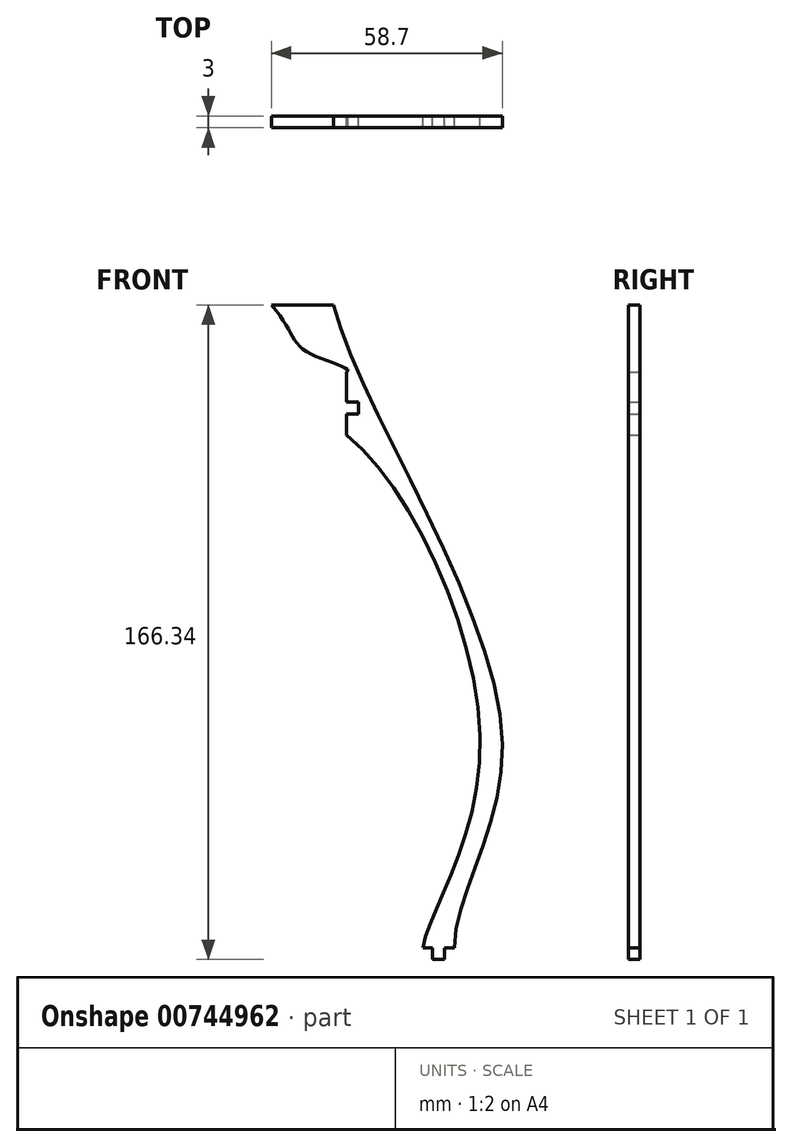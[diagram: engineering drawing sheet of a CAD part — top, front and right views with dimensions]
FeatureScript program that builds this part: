
annotation { "Feature Type Name" : "Feature", "Feature Type Description" : "" }
export const myFeature = defineFeature(function(context is Context, id is Id, definition is map)
    precondition{}
    {
        {
            var Q0;
            Q0=qCreatedBy(makeId("Front.planeOp"),FACE);
            var sketch = newSketch(context, id + "F0", { "sketchPlane" : qUnion([Q0])});
            skLineSegment(sketch, "E0", {"start": v(21.9, 51.28) * mm, "end": v(37.73, 51.28) * mm});
            skFitSpline(sketch, "E1", {"points": [v(37.73, 51.28) * mm, v(80.45, -57.24) * mm, v(68.38, -112.06) * mm], "startDerivative": vector(32.2, -132.18) * mm, "endDerivative": vector(-1.43, -110.43) * mm});
            skLineSegment(sketch, "E2", {"start": v(68.38, -112.06) * mm, "end": v(60.38, -112.06) * mm});
            skFitSpline(sketch, "E3", {"points": [v(0, 22.24) * mm, v(34.05, 22.24) * mm, v(74.9, -59.68) * mm, v(60.38, -112.06) * mm], "startDerivative": vector(163.27, -73.62) * mm, "endDerivative": vector(-14.47, -87.67) * mm});
            skLineSegment(sketch, "E4", {"start": v(41, 35) * mm, "end": v(41, 34.2) * mm});
            skLineSegment(sketch, "E5", {"start": v(41, 35) * mm, "end": v(41, 26.61) * mm});
            skPoint(sketch, "E6.start.orphan", {"position": v(0, 51.28) * mm});
            skPoint(sketch, "E7.orphan", {"position": v(0, 48.13) * mm});
            skPoint(sketch, "E8.start.orphan", {"position": v(0, 31.7) * mm});
            skLineSegment(sketch, "E9.bottom", {"start": v(41, 26.61) * mm, "end": v(44, 26.61) * mm});
            skLineSegment(sketch, "E9.top", {"start": v(41, 23.61) * mm, "end": v(44, 23.61) * mm});
            skLineSegment(sketch, "E9.right", {"start": v(44, 26.61) * mm, "end": v(44, 23.61) * mm});
            skLineSegment(sketch, "E10.trimOffspring", {"start": v(41, 23.61) * mm, "end": v(41, 18.21) * mm});
            skFitSpline(sketch, "E11", {"points": [v(21.9, 51.28) * mm, v(31.33, 39.12) * mm, v(41, 34.2) * mm], "startDerivative": vector(29.94, -33.73) * mm, "endDerivative": vector(-13.48, -6.74) * mm});
            skLineSegment(sketch, "E12", {"start": v(0, -62.73) * mm, "end": v(0, -105.6) * mm});
            skSolve(sketch);
        }
        {
            var Q0;
            Q0=makeQuery(id+"F0.imprint","IMPRINT",FACE,{"disambiguationData":[TD([[makeQuery(id+"F0.imprint","IMPRINT",EDGE,{"derivedFrom":sQuery(id+"F0.wireOp",EDGE,"E0")}),-1.0]])]});
            extrude(context, id + "F1", {"entities" : qUnion([Q0]), "depth" : 3 * mm, "offsetDistance" : 25 * mm});
        }
        {
            var Q0;
            Q0=qCreatedBy(makeId("Front.planeOp"),FACE);
            var sketch = newSketch(context, id + "F2", { "sketchPlane" : qUnion([Q0])});
            skLineSegment(sketch, "E13.bottom", {"start": v(62.88, -112.06) * mm, "end": v(65.88, -112.06) * mm});
            skLineSegment(sketch, "E13.top", {"start": v(62.88, -115.06) * mm, "end": v(65.88, -115.06) * mm});
            skLineSegment(sketch, "E13.left", {"start": v(62.88, -112.06) * mm, "end": v(62.88, -115.06) * mm});
            skLineSegment(sketch, "E13.right", {"start": v(65.88, -112.06) * mm, "end": v(65.88, -115.06) * mm});
            skLineSegment(sketch, "E14", {"start": v(60.38, -109.8) * mm, "end": v(60.38, -115.6) * mm, "construction": true});
            skLineSegment(sketch, "E15", {"start": v(58.7, -109.7) * mm, "end": v(58.7, -115.43) * mm, "construction": true});
            skSolve(sketch);
        }
        {
            var Q0;
            Q0=makeQuery(id+"F2.imprint","IMPRINT",FACE,{"disambiguationData":[TD([[makeQuery(id+"F2.imprint","IMPRINT",EDGE,{"derivedFrom":sQuery(id+"F2.wireOp",EDGE,"E13.bottom")}),-1.0]])]});
            extrude(context, id + "F3", {"entities" : qUnion([Q0]), "operationType" : NewBodyOperationType.ADD, "depth" : 3 * mm, "offsetDistance" : 25 * mm});
        }
    });
